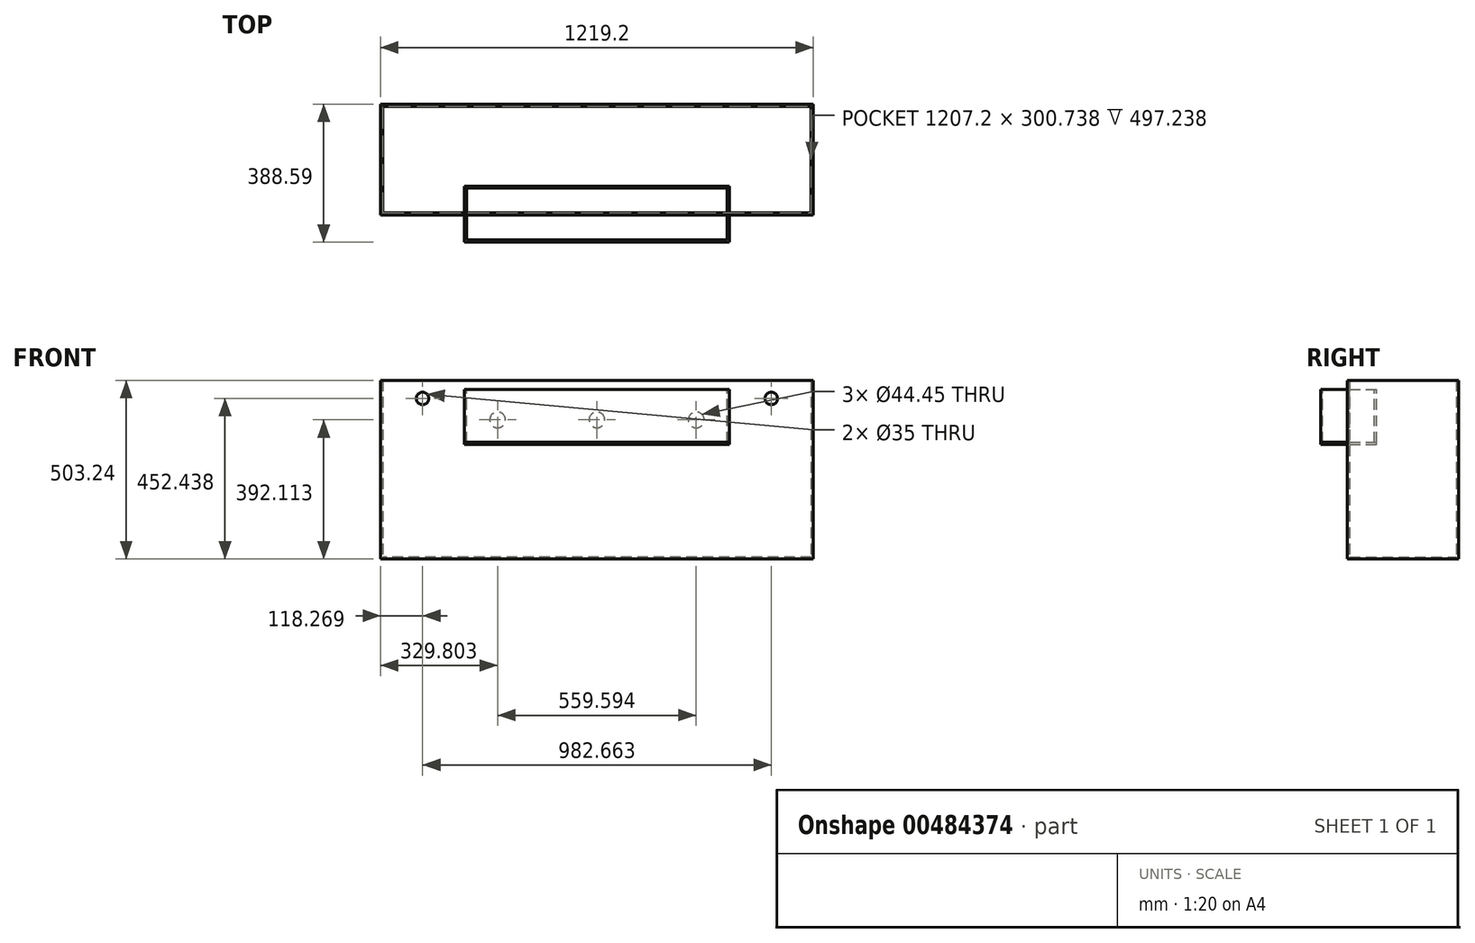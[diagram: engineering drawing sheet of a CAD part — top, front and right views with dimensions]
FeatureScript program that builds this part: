
annotation { "Feature Type Name" : "Feature", "Feature Type Description" : "" }
export const myFeature = defineFeature(function(context is Context, id is Id, definition is map)
    precondition{}
    {
        {
            var Q0;
            Q0=qCreatedBy(makeId("Top.planeOp"),FACE);
            var sketch = newSketch(context, id + "F0", { "sketchPlane" : qUnion([Q0])});
            skLineSegment(sketch, "E0.bottom", {"start": v(609.6, -156.37) * mm, "end": v(-609.6, -156.37) * mm});
            skLineSegment(sketch, "E0.top", {"start": v(609.6, 156.37) * mm, "end": v(-609.6, 156.37) * mm});
            skLineSegment(sketch, "E0.left", {"start": v(609.6, -156.37) * mm, "end": v(609.6, 156.37) * mm});
            skLineSegment(sketch, "E0.right", {"start": v(-609.6, -156.37) * mm, "end": v(-609.6, 156.37) * mm});
            skPoint(sketch, "E0.middle", {"position": v(0, 0) * mm});
            skSolve(sketch);
        }
        {
            var Q0;
            Q0=makeQuery(id+"F0.imprint","IMPRINT",FACE,{"disambiguationData":[TD([[makeQuery(id+"F0.imprint","IMPRINT",EDGE,{"derivedFrom":sQuery(id+"F0.wireOp",EDGE,"E0.bottom")}),-1.0]])]});
            extrude(context, id + "F1", {"entities" : qUnion([Q0]), "depth" : 503.24 * mm});
        }
        {
            var Q0;
            Q0=makeQuery(id+"F1.opExtrude","CAP_FACE",FACE,{"disambiguationData":[OSD([sQuery(id+"F0.wireOp",EDGE,"E0.bottom"),sQuery(id+"F0.wireOp",EDGE,"E0.top"),sQuery(id+"F0.wireOp",EDGE,"E0.left"),sQuery(id+"F0.wireOp",EDGE,"E0.right")])],"isStart":false});
            shell(context, id + "F2", {"entities" : qUnion([Q0]), "thickness" : 6 * mm});
        }
        {
            var Q0;
            Q0=makeQuery(id+"F1.opExtrude","SWEPT_FACE",FACE,{"disambiguationData":[OSD([sQuery(id+"F0.wireOp",EDGE,"E0.bottom")])]});
            var sketch = newSketch(context, id + "F3", { "sketchPlane" : qUnion([Q0])});
            skPoint(sketch, "E1", {"position": v(609.6, 414.34) * mm});
            skPoint(sketch, "E2", {"position": v(-609.6, 414.34) * mm});
            skLineSegment(sketch, "E3", {"start": v(-609.6, 414.34) * mm, "end": v(609.6, 414.34) * mm, "construction": true});
            skLineSegment(sketch, "E4", {"start": v(0, 503.24) * mm, "end": v(0, 0) * mm, "construction": true});
            skLineSegment(sketch, "E5", {"start": v(-609.6, 369.89) * mm, "end": v(609.6, 369.89) * mm, "construction": true});
            skLineSegment(sketch, "E6", {"start": v(-373.06, 503.24) * mm, "end": v(-373.06, 0) * mm, "construction": true});
            skLineSegment(sketch, "E7", {"start": v(373.06, 503.24) * mm, "end": v(373.06, 0) * mm, "construction": true});
            skLineSegment(sketch, "E8", {"start": v(0, 414.34) * mm, "end": v(0, 369.89) * mm, "construction": true});
            skPoint(sketch, "E9", {"position": v(0, 392.11) * mm});
            skLineSegment(sketch, "E10", {"start": v(-609.6, 392.11) * mm, "end": v(609.6, 392.11) * mm, "construction": true});
            skCircle(sketch, "E11", {"center": v(0, 392.11) * mm, "radius": 22.22 * mm});
            skLineSegment(sketch, "E12", {"start": v(0, 414.34) * mm, "end": v(-373.06, 414.34) * mm, "construction": true});
            skPoint(sketch, "E13", {"position": v(-186.53, 414.34) * mm});
            skLineSegment(sketch, "E14", {"start": v(-186.53, 414.34) * mm, "end": v(-186.53, 369.89) * mm, "construction": true});
            skLineSegment(sketch, "E15", {"start": v(0, 414.34) * mm, "end": v(373.06, 414.34) * mm, "construction": true});
            skPoint(sketch, "E16", {"position": v(186.53, 414.34) * mm});
            skLineSegment(sketch, "E17", {"start": v(186.53, 414.34) * mm, "end": v(186.53, 369.89) * mm, "construction": true});
            skLineSegment(sketch, "E18", {"start": v(-186.53, 414.34) * mm, "end": v(-373.06, 414.34) * mm, "construction": true});
            skPoint(sketch, "E19", {"position": v(-279.8, 414.34) * mm});
            skLineSegment(sketch, "E20", {"start": v(-279.8, 414.34) * mm, "end": v(-279.8, 369.89) * mm, "construction": true});
            skCircle(sketch, "E21", {"center": v(-279.8, 392.11) * mm, "radius": 22.23 * mm});
            skLineSegment(sketch, "E22", {"start": v(186.53, 414.34) * mm, "end": v(373.06, 414.34) * mm, "construction": true});
            skPoint(sketch, "E23", {"position": v(279.8, 414.34) * mm});
            skLineSegment(sketch, "E24", {"start": v(279.8, 414.34) * mm, "end": v(279.8, 369.89) * mm, "construction": true});
            skCircle(sketch, "E25", {"center": v(279.8, 392.11) * mm, "radius": 22.22 * mm});
            skLineSegment(sketch, "E26", {"start": v(-609.6, 328.61) * mm, "end": v(609.6, 328.61) * mm, "construction": true});
            skLineSegment(sketch, "E27", {"start": v(373.06, 503.24) * mm, "end": v(609.6, 503.24) * mm, "construction": true});
            skLineSegment(sketch, "E28", {"start": v(491.33, 503.24) * mm, "end": v(491.33, 0) * mm, "construction": true});
            skLineSegment(sketch, "E29", {"start": v(-609.6, 503.24) * mm, "end": v(-373.06, 503.24) * mm, "construction": true});
            skLineSegment(sketch, "E30", {"start": v(-491.33, 503.24) * mm, "end": v(-491.33, 0) * mm, "construction": true});
            skLineSegment(sketch, "E31", {"start": v(-609.6, 503.24) * mm, "end": v(-609.6, 414.34) * mm, "construction": true});
            skCircle(sketch, "E32", {"center": v(491.33, 452.44) * mm, "radius": 17.5 * mm});
            skLineSegment(sketch, "E33", {"start": v(-609.6, 452.44) * mm, "end": v(609.6, 452.44) * mm, "construction": true});
            skCircle(sketch, "E34", {"center": v(-491.33, 452.44) * mm, "radius": 17.5 * mm});
            skSolve(sketch);
        }
        {
            var Q0;
            Q0=makeQuery(id+"F1.opExtrude","CAP_FACE",FACE,{"disambiguationData":[OSD([sQuery(id+"F0.wireOp",EDGE,"E0.bottom"),sQuery(id+"F0.wireOp",EDGE,"E0.top"),sQuery(id+"F0.wireOp",EDGE,"E0.left"),sQuery(id+"F0.wireOp",EDGE,"E0.right")])],"isStart":false});
            var sketch = newSketch(context, id + "F4", { "sketchPlane" : qUnion([Q0])});
            skLineSegment(sketch, "E35", {"start": v(-603.6, -80.52) * mm, "end": v(603.6, -80.52) * mm, "construction": true});
            skPoint(sketch, "E36.0", {"position": v(373.06, -156.37) * mm});
            skPoint(sketch, "E37.0", {"position": v(-373.06, -156.37) * mm});
            skLineSegment(sketch, "E38", {"start": v(-373.06, -156.37) * mm, "end": v(-373.06, -80.52) * mm, "construction": true});
            skLineSegment(sketch, "E39", {"start": v(373.06, -156.37) * mm, "end": v(373.06, -80.52) * mm, "construction": true});
            skPoint(sketch, "E40", {"position": v(-373.06, -150.37) * mm});
            skPoint(sketch, "E41", {"position": v(-367.06, -150.37) * mm});
            skPoint(sketch, "E42", {"position": v(367.06, -150.37) * mm});
            skLineSegment(sketch, "E43", {"start": v(367.06, -150.37) * mm, "end": v(367.06, -80.52) * mm, "construction": true});
            skLineSegment(sketch, "E44.bottom", {"start": v(-373.06, -80.52) * mm, "end": v(373.06, -80.52) * mm});
            skLineSegment(sketch, "E44.top", {"start": v(-373.06, -74.52) * mm, "end": v(373.06, -74.52) * mm});
            skLineSegment(sketch, "E44.left", {"start": v(-373.06, -80.52) * mm, "end": v(-373.06, -74.52) * mm});
            skLineSegment(sketch, "E44.right", {"start": v(373.06, -80.52) * mm, "end": v(373.06, -74.52) * mm});
            skLineSegment(sketch, "E45.left", {"start": v(-373.06, -74.52) * mm, "end": v(-373.06, -80.52) * mm});
            skLineSegment(sketch, "E45.right", {"start": v(373.06, -74.52) * mm, "end": v(373.06, -80.52) * mm});
            skLineSegment(sketch, "E46.bottom", {"start": v(-367.06, -150.37) * mm, "end": v(-373.06, -150.37) * mm});
            skLineSegment(sketch, "E46.top", {"start": v(-367.06, -80.52) * mm, "end": v(-373.06, -80.52) * mm});
            skLineSegment(sketch, "E46.left", {"start": v(-367.06, -150.37) * mm, "end": v(-367.06, -80.52) * mm});
            skLineSegment(sketch, "E46.right", {"start": v(-373.06, -150.37) * mm, "end": v(-373.06, -80.52) * mm});
            skLineSegment(sketch, "E47.bottom", {"start": v(367.06, -150.37) * mm, "end": v(373.06, -150.37) * mm});
            skLineSegment(sketch, "E47.top", {"start": v(367.06, -80.52) * mm, "end": v(373.06, -80.52) * mm});
            skLineSegment(sketch, "E47.left", {"start": v(367.06, -150.37) * mm, "end": v(367.06, -80.52) * mm});
            skLineSegment(sketch, "E47.right", {"start": v(373.06, -150.37) * mm, "end": v(373.06, -80.52) * mm});
            skSolve(sketch);
        }
        {
            var Q0;
            Q0=makeQuery(id+"F4.imprint","IMPRINT",FACE,{"disambiguationData":[TD([[makeQuery(id+"F4.imprint","IMPRINT",EDGE,{"derivedFrom":sQuery(id+"F4.wireOp",EDGE,"E47.bottom")}),-1.0]])]});
            var Q1;
            Q1=makeQuery(id+"F4.imprint","IMPRINT",FACE,{"disambiguationData":[TD([[makeQuery(id+"F4.imprint","IMPRINT",EDGE,{"derivedFrom":sQuery(id+"F4.wireOp",EDGE,"E44.top")}),-1.0]])]});
            var Q2;
            Q2=makeQuery(id+"F4.imprint","IMPRINT",FACE,{"disambiguationData":[TD([[makeQuery(id+"F4.imprint","IMPRINT",EDGE,{"derivedFrom":sQuery(id+"F4.wireOp",EDGE,"E46.bottom")}),-1.0]])]});
            extrude(context, id + "F5", {"entities" : qUnion([Q0, Q1, Q2]), "oppositeDirection" : true, "depth" : 174.62 * mm});
        }
        {
            var Q0;
            Q0=makeQuery(id+"F5.opExtrude","CAP_FACE",FACE,{"disambiguationData":[OSD([sQuery(id+"F4.wireOp",EDGE,"E44.top"),sQuery(id+"F4.wireOp",EDGE,"E44.bottom"),sQuery(id+"F4.wireOp",EDGE,"E45.left"),sQuery(id+"F4.wireOp",EDGE,"E45.right"),sQuery(id+"F4.wireOp",EDGE,"E46.bottom"),sQuery(id+"F4.wireOp",EDGE,"E46.left"),sQuery(id+"F4.wireOp",EDGE,"E46.right"),sQuery(id+"F4.wireOp",EDGE,"E47.bottom"),sQuery(id+"F4.wireOp",EDGE,"E47.left"),sQuery(id+"F4.wireOp",EDGE,"E47.right")])],"isStart":true});
            extrude(context, id + "F6", {"entities" : qUnion([Q0]), "operationType" : NewBodyOperationType.REMOVE, "oppositeDirection" : true, "depth" : 25.4 * mm});
        }
        {
            var Q0;
            Q0=makeQuery(id+"F5.opExtrude","CAP_FACE",FACE,{"disambiguationData":[OSD([sQuery(id+"F4.wireOp",EDGE,"E44.top"),sQuery(id+"F4.wireOp",EDGE,"E44.bottom"),sQuery(id+"F4.wireOp",EDGE,"E45.left"),sQuery(id+"F4.wireOp",EDGE,"E45.right"),sQuery(id+"F4.wireOp",EDGE,"E46.bottom"),sQuery(id+"F4.wireOp",EDGE,"E46.left"),sQuery(id+"F4.wireOp",EDGE,"E46.right"),sQuery(id+"F4.wireOp",EDGE,"E47.bottom"),sQuery(id+"F4.wireOp",EDGE,"E47.left"),sQuery(id+"F4.wireOp",EDGE,"E47.right")])],"isStart":false});
            var sketch = newSketch(context, id + "F7", { "sketchPlane" : qUnion([Q0])});
            skLineSegment(sketch, "E48.bottom", {"start": v(-373.06, 150.37) * mm, "end": v(373.06, 150.37) * mm});
            skLineSegment(sketch, "E48.top", {"start": v(-373.06, 74.52) * mm, "end": v(373.06, 74.52) * mm});
            skLineSegment(sketch, "E48.left", {"start": v(-373.06, 150.37) * mm, "end": v(-373.06, 74.52) * mm});
            skLineSegment(sketch, "E48.right", {"start": v(373.06, 150.37) * mm, "end": v(373.06, 74.52) * mm});
            skSolve(sketch);
        }
        {
            var Q0;
            Q0 = qSketchRegion(id + "F7", true);
            extrude(context, id + "F8", {"entities" : qUnion([Q0]), "depth" : 6 * mm});
        }
        {
            var Q0;
            Q0=makeQuery(id+"F3.imprint","IMPRINT",FACE,{"disambiguationData":[TD([[makeQuery(id+"F3.imprint","IMPRINT",EDGE,{"derivedFrom":sQuery(id+"F3.wireOp",EDGE,"E25")}),1.0]])]});
            var Q1;
            Q1=makeQuery(id+"F3.imprint","IMPRINT",FACE,{"disambiguationData":[TD([[makeQuery(id+"F3.imprint","IMPRINT",EDGE,{"derivedFrom":sQuery(id+"F3.wireOp",EDGE,"E11")}),1.0]])]});
            var Q2;
            Q2=makeQuery(id+"F3.imprint","IMPRINT",FACE,{"disambiguationData":[TD([[makeQuery(id+"F3.imprint","IMPRINT",EDGE,{"derivedFrom":sQuery(id+"F3.wireOp",EDGE,"E21")}),1.0]])]});
            var Q3;
            Q3=sQuery(id+"F3.wireOp",EDGE,"E21");
            var Q4;
            Q4=sQuery(id+"F3.wireOp",EDGE,"E11");
            var Q5;
            Q5=sQuery(id+"F3.wireOp",EDGE,"E25");
            var Q6;
            Q6=makeQuery(id+"F5.opExtrude","SWEPT_BODY",BODY,{"disambiguationData":[OSD([sQuery(id+"F4.wireOp",EDGE,"E44.top"),sQuery(id+"F4.wireOp",EDGE,"E44.bottom"),sQuery(id+"F4.wireOp",EDGE,"E45.left"),sQuery(id+"F4.wireOp",EDGE,"E45.right"),sQuery(id+"F4.wireOp",EDGE,"E46.bottom"),sQuery(id+"F4.wireOp",EDGE,"E46.left"),sQuery(id+"F4.wireOp",EDGE,"E46.right"),sQuery(id+"F4.wireOp",EDGE,"E47.bottom"),sQuery(id+"F4.wireOp",EDGE,"E47.left"),sQuery(id+"F4.wireOp",EDGE,"E47.right")])]});
            extrude(context, id + "F9", {"entities" : qUnion([Q0, Q1, Q2]), "operationType" : NewBodyOperationType.REMOVE, "surfaceEntities" : qUnion([Q3, Q4, Q5]), "endBound" : BoundingType.UP_TO_BODY, "oppositeDirection" : true, "endBoundEntityBody" : qUnion([Q6]), "depth" : 25.4 * mm});
        }
        {
            var Q0;
            Q0=makeQuery(id+"F3.imprint","IMPRINT",FACE,{"disambiguationData":[TD([[makeQuery(id+"F3.imprint","IMPRINT",EDGE,{"derivedFrom":sQuery(id+"F3.wireOp",EDGE,"E34")}),1.0]])]});
            var Q1;
            Q1=makeQuery(id+"F3.imprint","IMPRINT",FACE,{"disambiguationData":[TD([[makeQuery(id+"F3.imprint","IMPRINT",EDGE,{"derivedFrom":sQuery(id+"F3.wireOp",EDGE,"E32")}),1.0]])]});
            var Q2;
            Q2=sQuery(id+"F3.wireOp",EDGE,"E34");
            var Q3;
            Q3=sQuery(id+"F3.wireOp",EDGE,"E32");
            var Q4;
            Q4=makeQuery(id+"F1.opExtrude","SWEPT_BODY",BODY,{"disambiguationData":[OSD([sQuery(id+"F0.wireOp",EDGE,"E0.bottom"),sQuery(id+"F0.wireOp",EDGE,"E0.top"),sQuery(id+"F0.wireOp",EDGE,"E0.left"),sQuery(id+"F0.wireOp",EDGE,"E0.right")])]});
            extrude(context, id + "F10", {"entities" : qUnion([Q0, Q1]), "operationType" : NewBodyOperationType.REMOVE, "surfaceEntities" : qUnion([Q2, Q3]), "endBound" : BoundingType.UP_TO_BODY, "oppositeDirection" : true, "endBoundEntityBody" : qUnion([Q4]), "depth" : 25.4 * mm});
        }
        {
            var Q0;
            Q0=makeQuery(id+"F5.opExtrude","SWEPT_BODY",BODY,{"disambiguationData":[OSD([sQuery(id+"F4.wireOp",EDGE,"E44.top"),sQuery(id+"F4.wireOp",EDGE,"E44.bottom"),sQuery(id+"F4.wireOp",EDGE,"E45.left"),sQuery(id+"F4.wireOp",EDGE,"E45.right"),sQuery(id+"F4.wireOp",EDGE,"E46.bottom"),sQuery(id+"F4.wireOp",EDGE,"E46.left"),sQuery(id+"F4.wireOp",EDGE,"E46.right"),sQuery(id+"F4.wireOp",EDGE,"E47.bottom"),sQuery(id+"F4.wireOp",EDGE,"E47.left"),sQuery(id+"F4.wireOp",EDGE,"E47.right")])]});
            var Q1;
            Q1=makeQuery(id+"F8.opExtrude","SWEPT_BODY",BODY,{"disambiguationData":[OSD([sQuery(id+"F7.wireOp",EDGE,"E48.bottom"),sQuery(id+"F7.wireOp",EDGE,"E48.top"),sQuery(id+"F7.wireOp",EDGE,"E48.left"),sQuery(id+"F7.wireOp",EDGE,"E48.right")])]});
            var Q2;
            Q2=makeQuery(id+"F3.imprint","IMPRINT",FACE,{"disambiguationData":[TD([[makeQuery(id+"F3.imprint","IMPRINT",EDGE,{"derivedFrom":sQuery(id+"F3.wireOp",EDGE,"E11")}),-1.0]])]});
            mirror(context, id + "F11", {"entities" : qUnion([Q0, Q1]), "mirrorPlane" : qUnion([Q2])});
        }
        {
            var Q0;
            Q0=makeQuery(id+"F11.opPattern","COPY",BODY,{"derivedFrom":makeQuery(id+"F5.opExtrude","SWEPT_BODY",BODY,{"disambiguationData":[OSD([sQuery(id+"F4.wireOp",EDGE,"E44.top"),sQuery(id+"F4.wireOp",EDGE,"E44.bottom"),sQuery(id+"F4.wireOp",EDGE,"E45.left"),sQuery(id+"F4.wireOp",EDGE,"E45.right"),sQuery(id+"F4.wireOp",EDGE,"E46.bottom"),sQuery(id+"F4.wireOp",EDGE,"E46.left"),sQuery(id+"F4.wireOp",EDGE,"E46.right"),sQuery(id+"F4.wireOp",EDGE,"E47.bottom"),sQuery(id+"F4.wireOp",EDGE,"E47.left"),sQuery(id+"F4.wireOp",EDGE,"E47.right")])]}),"instanceName":"1"});
            var Q1;
            Q1=makeQuery(id+"F11.opPattern","COPY",BODY,{"derivedFrom":makeQuery(id+"F8.opExtrude","SWEPT_BODY",BODY,{"disambiguationData":[OSD([sQuery(id+"F7.wireOp",EDGE,"E48.bottom"),sQuery(id+"F7.wireOp",EDGE,"E48.top"),sQuery(id+"F7.wireOp",EDGE,"E48.left"),sQuery(id+"F7.wireOp",EDGE,"E48.right")])]}),"instanceName":"1"});
            transform(context, id + "F12", {"entities" : qUnion([Q0, Q1]), "transformType" : TransformType.TRANSLATION_3D, "dx" : 0 * mm, "dy" : 6 * mm, "dz" : 0 * mm, "makeCopy" : false});
        }
    });
